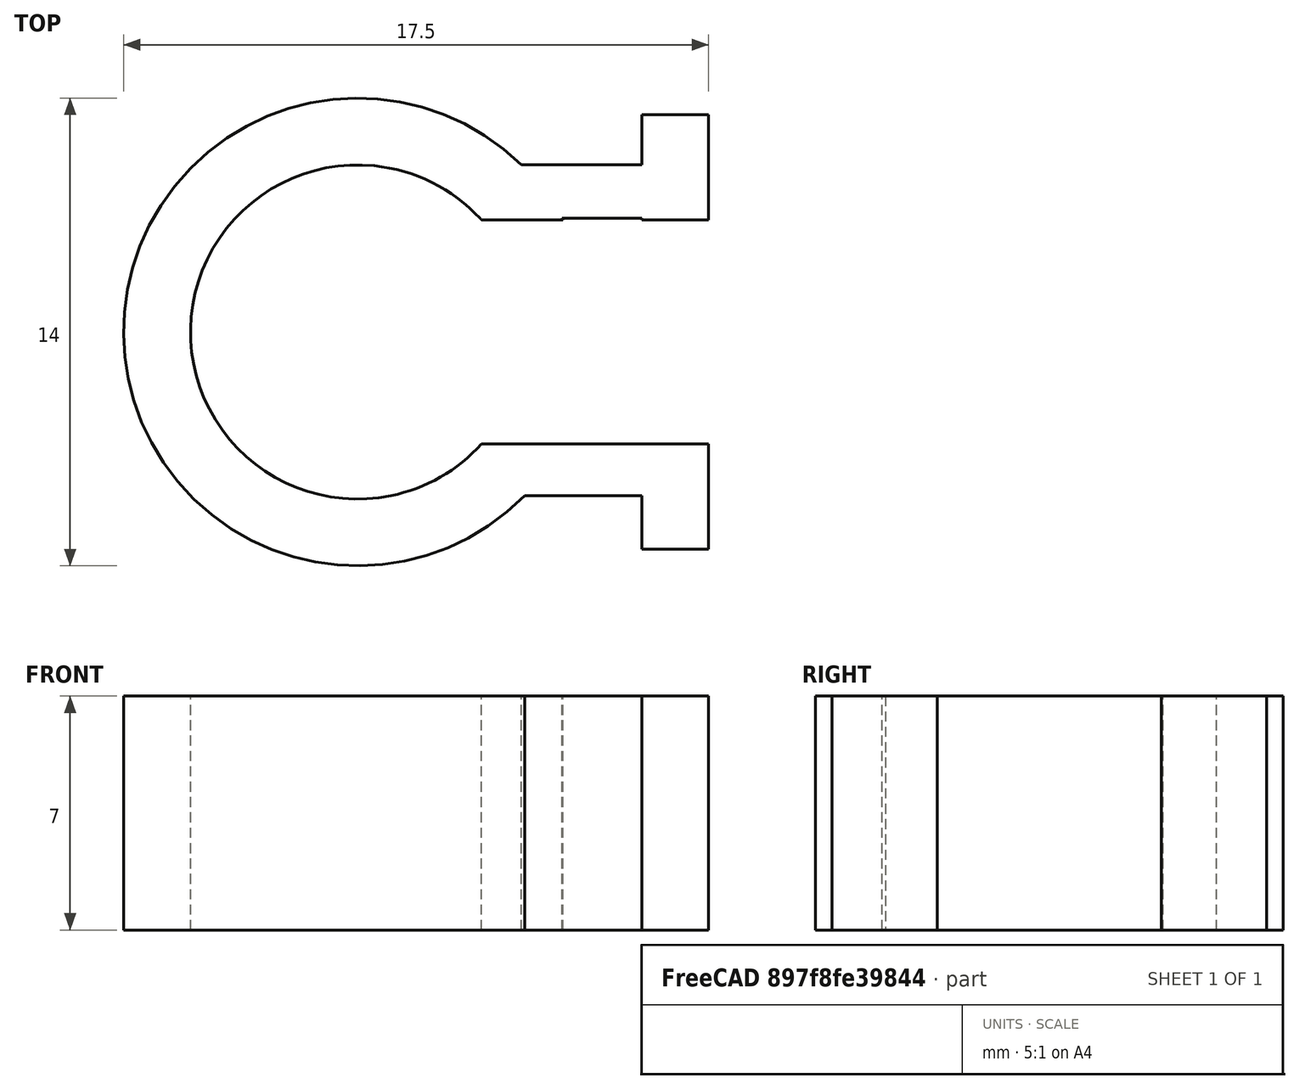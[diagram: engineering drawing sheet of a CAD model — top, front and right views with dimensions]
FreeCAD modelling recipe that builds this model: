
FCSTD DOCUMENT  (FreeCAD 0.18R16110 (Git))
Label: power-cable-clip
License: All rights reserved
LicenseURL: http://en.wikipedia.org/wiki/All_rights_reserved
objects: Part::Box×4, Part::Cylinder×2, Part::Cut×2, Part::MultiFuse×1, Mesh::Feature×1
note: 9 computed .brp shape members not serialized (recipe doc carries the construction recipe); baked Part::Feature solids carry a one-line shape summary decoded from their .brp

FEATURE [Part::Cylinder] Cylinder106  label="Zylinder094"
  Angle = 360
  AttacherType = Attacher::AttachEngine3D
  Height = 7
  Radius = 5
FEATURE [Part::Box] Box071  label="Quader050"
  AttacherType = Attacher::AttachEngine3D
  Height = 7
  Length = 10
  Placement = pos=(0.5,-4.9,0) rot=(0,0,1;0rad)
  Width = 1.6
FEATURE [Part::Box] Box070  label="Quader049"
  AttacherType = Attacher::AttachEngine3D
  Height = 7
  Length = 10
  Placement = pos=(0.5,-3.35,0) rot=(0,0,1;0rad)
  Width = 6.7
FEATURE [Part::Box] Box072  label="Quader051"
  AttacherType = Attacher::AttachEngine3D
  Height = 7
  Length = 10
  Placement = pos=(0.5,3.4,0) rot=(0,0,1;0rad)
  Width = 1.6
FEATURE [Part::Cylinder] Cylinder107  label="Zylinder095"
  Angle = 360
  AttacherType = Attacher::AttachEngine3D
  Height = 7
  Radius = 7
FEATURE [Part::Box] Box073  label="Quader052"
  AttacherType = Attacher::AttachEngine3D
  Height = 7
  Length = 2
  Placement = pos=(8.5,-6.5,0) rot=(0,0,1;0rad)
  Width = 13
FEATURE [Part::MultiFuse] Fusion052
  Shapes = -> [Box072,Box071,Cylinder107,Box073]
FEATURE [Part::Cut] Cut122
  Base = -> Fusion052
  Tool = -> Box070
FEATURE [Part::Cut] Cut123  label="power-cable-clip"
  Base = -> Cut122
  Tool = -> Cylinder106
FEATURE [Mesh::Feature] Mesh  label="power-cable-clip (Meshed)"
